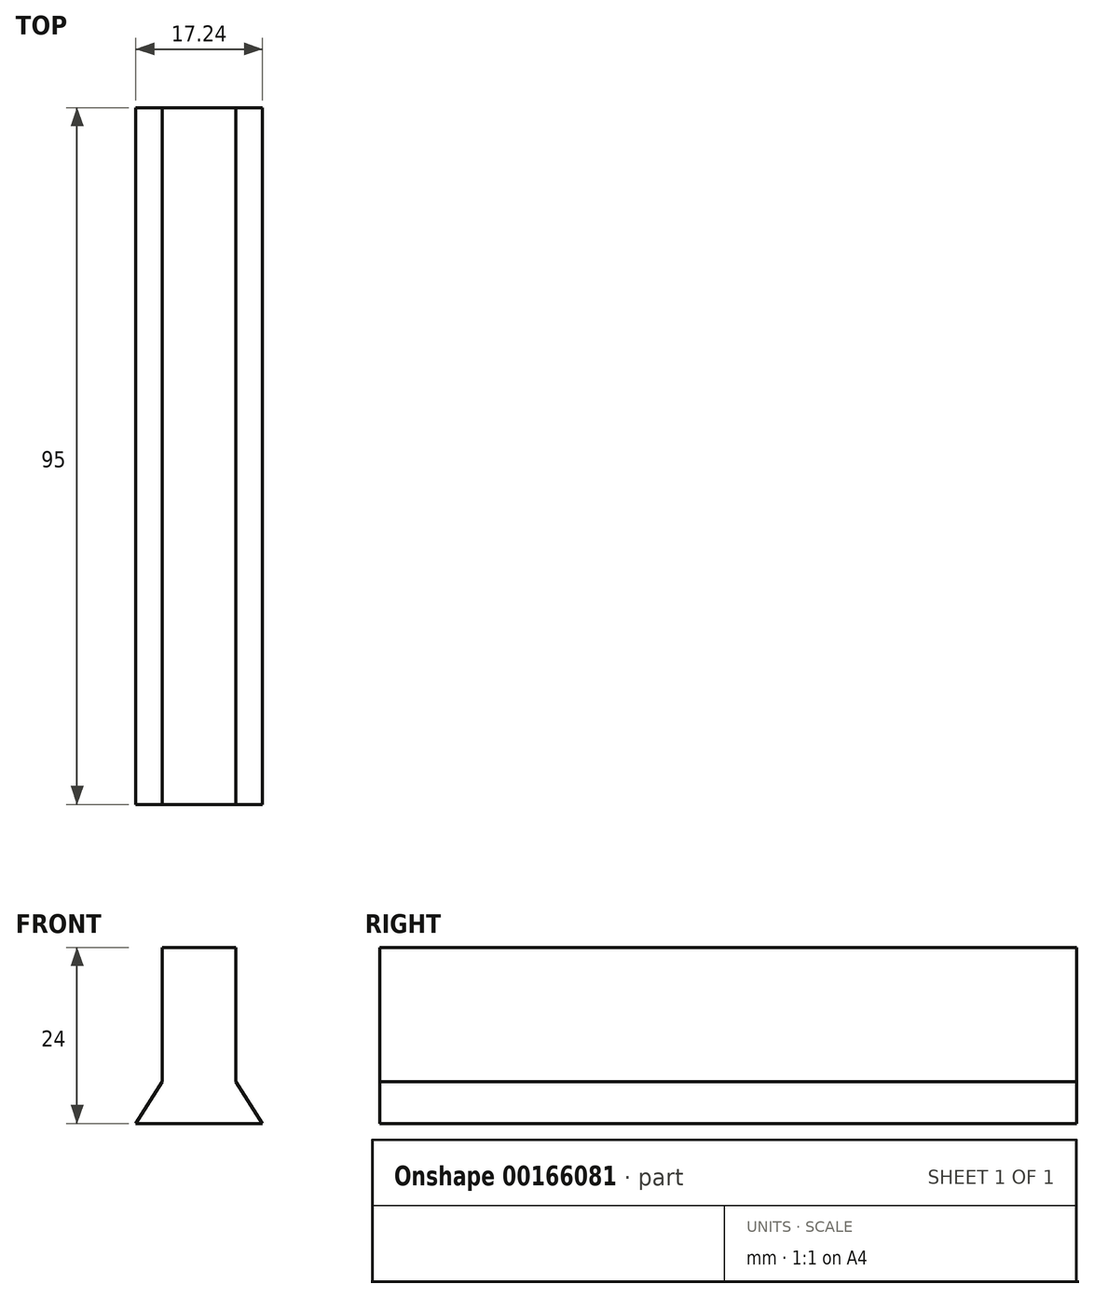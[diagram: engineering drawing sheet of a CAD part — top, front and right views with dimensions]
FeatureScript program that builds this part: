
annotation { "Feature Type Name" : "Feature", "Feature Type Description" : "" }
export const myFeature = defineFeature(function(context is Context, id is Id, definition is map)
    precondition{}
    {
        {
            var Q0;
            Q0=qCreatedBy(makeId("Front.planeOp"),FACE);
            var sketch = newSketch(context, id + "F0", { "sketchPlane" : qUnion([Q0])});
            skLineSegment(sketch, "E0.trimOffspring", {"start": v(5.76, 18) * mm, "end": v(15, 18) * mm});
            skLineSegment(sketch, "E1", {"start": v(5.76, 14) * mm, "end": v(5.76, 18) * mm});
            skLineSegment(sketch, "E2", {"start": v(15, 18) * mm, "end": v(15, 0) * mm});
            skLineSegment(sketch, "E3", {"start": v(5.76, 14) * mm, "end": v(10, 7.28) * mm});
            skLineSegment(sketch, "E4", {"start": v(10, 7.28) * mm, "end": v(0, 7.28) * mm});
            skLineSegment(sketch, "E5", {"start": v(15, 0) * mm, "end": v(0, 0) * mm});
            skLineSegment(sketch, "E6.MirrorCS", {"start": v(-5.76, 14) * mm, "end": v(-10, 7.28) * mm});
            skLineSegment(sketch, "E7.MirrorCS", {"start": v(-15, 18) * mm, "end": v(-15, 0) * mm});
            skLineSegment(sketch, "E8.MirrorCS", {"start": v(-5.76, 14) * mm, "end": v(-5.76, 18) * mm});
            skLineSegment(sketch, "E9.MirrorCS", {"start": v(-10, 7.28) * mm, "end": v(0, 7.28) * mm});
            skLineSegment(sketch, "E10.MirrorCS", {"start": v(-5.76, 18) * mm, "end": v(-15, 18) * mm});
            skLineSegment(sketch, "E11", {"start": v(-15, 0) * mm, "end": v(0, 0) * mm});
            skLineSegment(sketch, "E12", {"start": v(5.01, 32.28) * mm, "end": v(5.01, 14) * mm});
            skLineSegment(sketch, "E13", {"start": v(5.01, 14) * mm, "end": v(8.62, 8.28) * mm});
            skLineSegment(sketch, "E14", {"start": v(0, 8.28) * mm, "end": v(8.62, 8.28) * mm});
            skLineSegment(sketch, "E15", {"start": v(5.01, 32.28) * mm, "end": v(0, 32.28) * mm});
            skLineSegment(sketch, "E16.MirrorCS", {"start": v(0, 8.28) * mm, "end": v(-8.62, 8.28) * mm});
            skLineSegment(sketch, "E17.MirrorCS", {"start": v(-5.01, 32.28) * mm, "end": v(-5.01, 14) * mm});
            skLineSegment(sketch, "E18.MirrorCS", {"start": v(-5.01, 14) * mm, "end": v(-8.62, 8.28) * mm});
            skLineSegment(sketch, "E19.MirrorCS", {"start": v(-5.01, 32.28) * mm, "end": v(0, 32.28) * mm});
            skSolve(sketch);
        }
        {
            var Q0;
            Q0=makeQuery(id+"F0.imprint","IMPRINT",FACE,{"disambiguationData":[TD([[makeQuery(id+"F0.imprint","IMPRINT",EDGE,{"derivedFrom":sQuery(id+"F0.wireOp",EDGE,"E12")}),-1.0]])]});
            extrude(context, id + "F1", {"entities" : qUnion([Q0]), "endBound" : BoundingType.SYMMETRIC, "depth" : 95 * mm});
        }
    });
